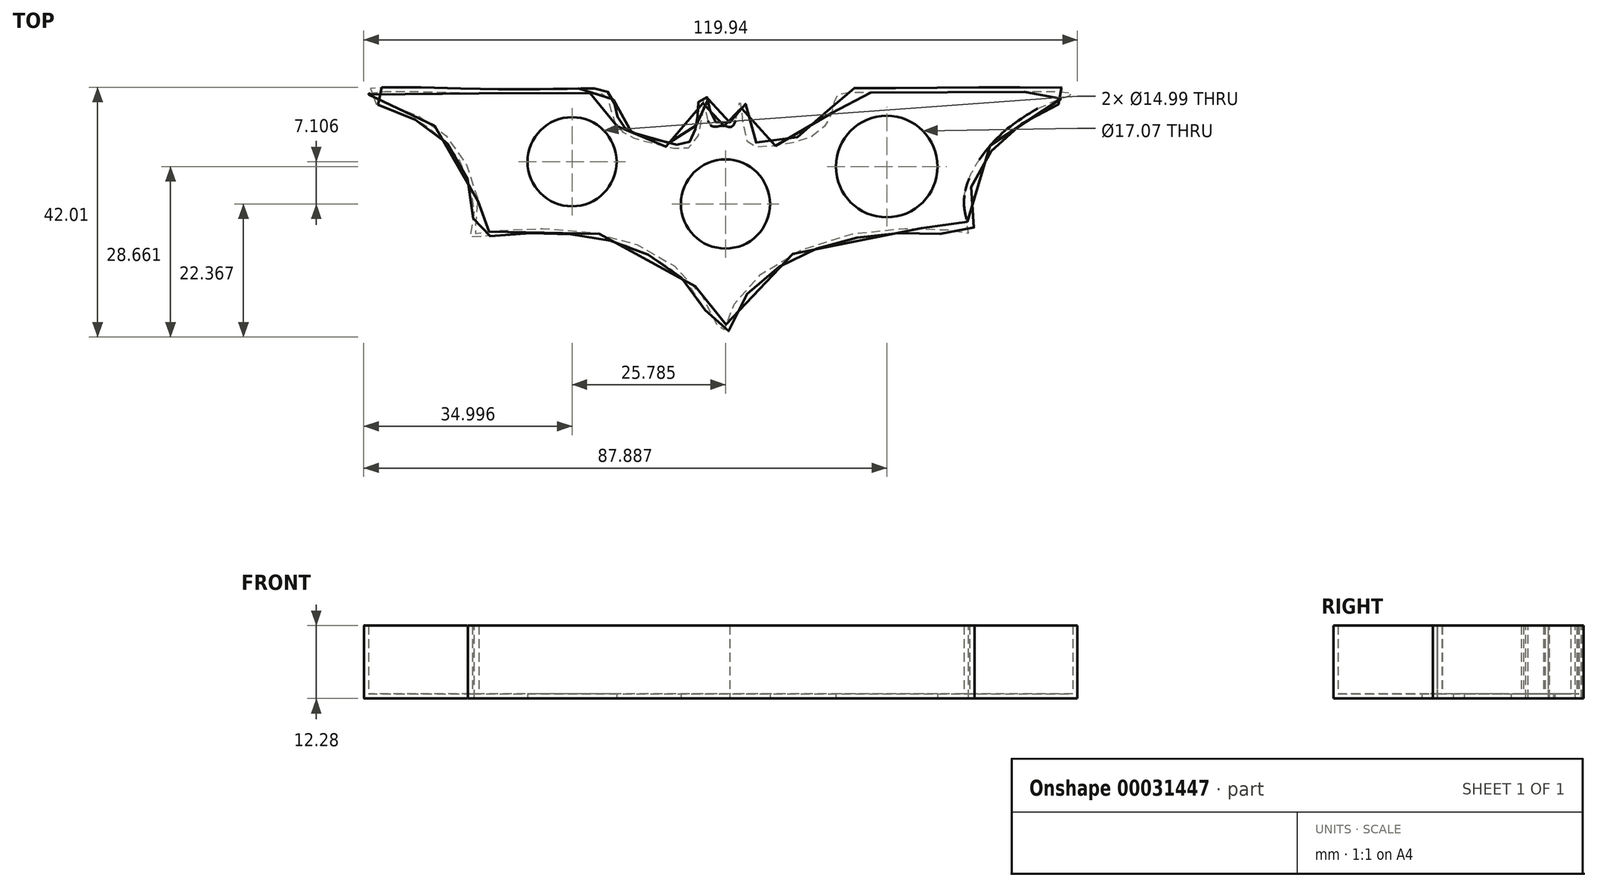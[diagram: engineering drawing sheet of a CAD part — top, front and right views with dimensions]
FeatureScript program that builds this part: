
annotation { "Feature Type Name" : "Feature", "Feature Type Description" : "" }
export const myFeature = defineFeature(function(context is Context, id is Id, definition is map)
    precondition{}
    {
        {
            var Q0;
            Q0=qCreatedBy(makeId("Top.planeOp"),FACE);
            var sketch = newSketch(context, id + "F0", { "sketchPlane" : qUnion([Q0])});
            skFitSpline(sketch, "E0", {"points": [v(-63.62, 25.23) * mm, v(-57.35, 22.54) * mm, v(-48.4, 15.64) * mm, v(-45.2, 4.5) * mm, v(-46.14, 2.02) * mm, v(-42.77, 2.2) * mm, v(-22.56, 1.31) * mm, v(-7.6, -8.54) * mm, v(-4.15, -14.8) * mm, v(-2.26, -10.24) * mm, v(15.11, 1.2) * mm, v(35.81, 2.15) * mm, v(37.44, 2.05) * mm, v(36.48, 6.75) * mm, v(41.66, 17.48) * mm, v(51.62, 24.1) * mm, v(54.78, 25.31) * mm, v(52.1, 25.63) * mm, v(19.62, 25.53) * mm, v(14.97, 24.9) * mm, v(14.35, 22.46) * mm, v(11.28, 18.34) * mm, v(2.42, 16.4) * mm, v(0, 17.5) * mm, v(-1.17, 24.28) * mm, v(-2.31, 20.01) * mm, v(-4.03, 19.95) * mm, v(-6.16, 20.11) * mm, v(-7.3, 24.33) * mm, v(-8.82, 16.99) * mm, v(-14.5, 16.65) * mm, v(-18.9, 17.79) * mm, v(-22.12, 20.43) * mm, v(-23.45, 24.66) * mm, v(-25.77, 25.44) * mm, v(-43.41, 25.36) * mm, v(-63.62, 25.23) * mm]});
            skSolve(sketch);
        }
        {
            var Q0;
            Q0 = qSketchRegion(id + "F0", true);
            extrude(context, id + "F1", {"entities" : qUnion([Q0]), "depth" : 11.52 * mm});
        }
        {
            var Q0;
            Q0=makeQuery(id+"F1.opExtrude","CAP_FACE",FACE,{"disambiguationData":[OSD([sQuery(id+"F0.wireOp",EDGE,"E0")])],"isStart":false});
            shell(context, id + "F2", {"entities" : qUnion([Q0]), "thickness" : 0.76 * mm, "oppositeDirection" : true});
        }
        {
            var Q0;
            Q0=makeQuery(id+"F1.opExtrude","CAP_FACE",FACE,{"disambiguationData":[OSD([sQuery(id+"F0.wireOp",EDGE,"E0")])],"isStart":true});
            var sketch = newSketch(context, id + "F3", { "sketchPlane" : qUnion([Q0])});
            skCircle(sketch, "E1", {"center": v(23.5, -13.1) * mm, "radius": 8.54 * mm});
            skCircle(sketch, "E2", {"center": v(-3.6, -6.8) * mm, "radius": 7.5 * mm});
            skCircle(sketch, "E3", {"center": v(-29.4, -13.9) * mm, "radius": 7.5 * mm});
            skSolve(sketch);
        }
        {
            var Q0;
            Q0=makeQuery(id+"F3.imprint","IMPRINT",FACE,{"disambiguationData":[TD([[makeQuery(id+"F3.imprint","IMPRINT",EDGE,{"derivedFrom":sQuery(id+"F3.wireOp",EDGE,"E1")}),1.0]])]});
            extrude(context, id + "F4", {"entities" : qUnion([Q0]), "operationType" : NewBodyOperationType.REMOVE, "oppositeDirection" : true, "depth" : 25.4 * mm});
        }
        {
            var Q0;
            Q0 = qSketchRegion(id + "F3", true);
            extrude(context, id + "F5", {"entities" : qUnion([Q0]), "operationType" : NewBodyOperationType.REMOVE, "oppositeDirection" : true, "depth" : 25.4 * mm});
        }
    });
